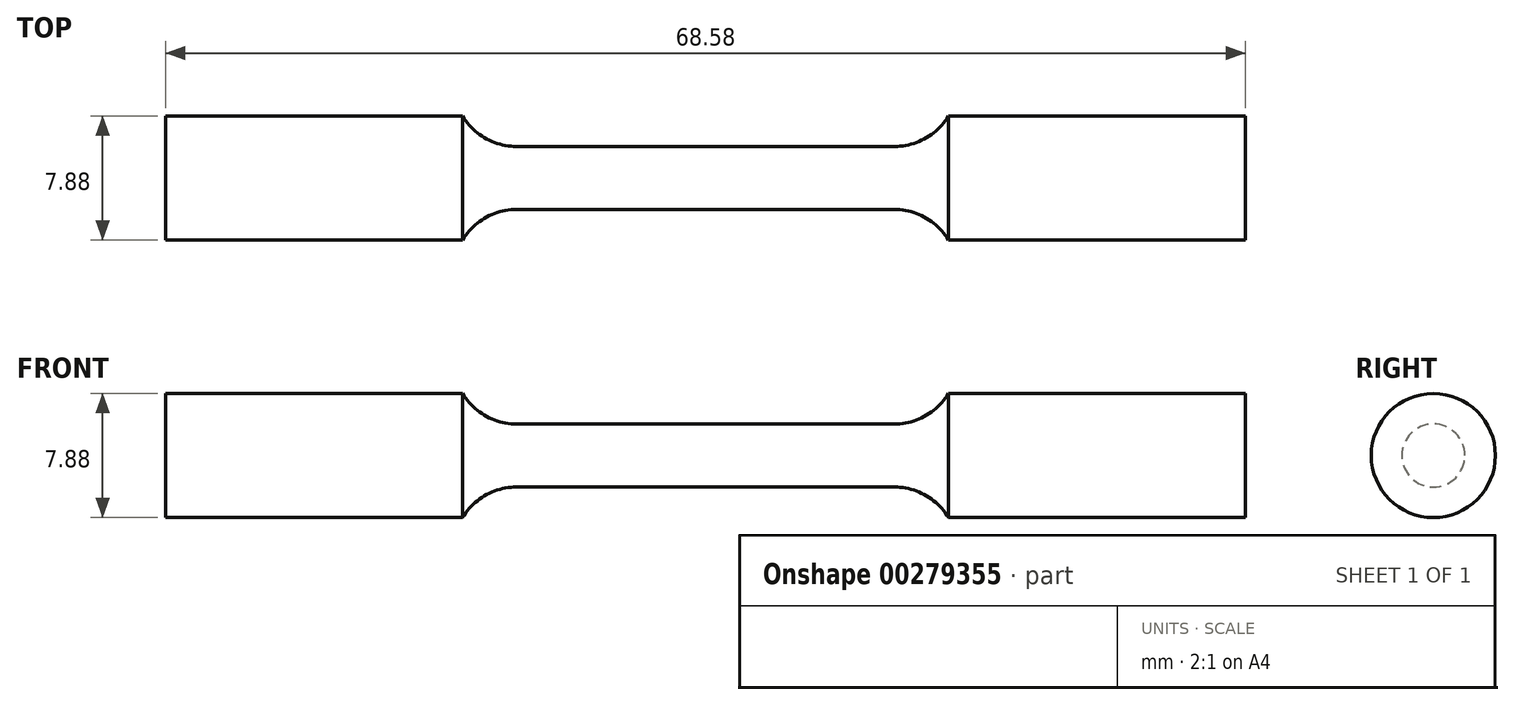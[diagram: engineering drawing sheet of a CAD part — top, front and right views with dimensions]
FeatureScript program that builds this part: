
annotation { "Feature Type Name" : "Feature", "Feature Type Description" : "" }
export const myFeature = defineFeature(function(context is Context, id is Id, definition is map)
    precondition{}
    {
        {
            var Q0;
            Q0=qCreatedBy(makeId("Front.planeOp"),FACE);
            var sketch = newSketch(context, id + "F0", { "sketchPlane" : qUnion([Q0])});
            skLineSegment(sketch, "E0", {"start": v(0, 2) * mm, "end": v(12, 2) * mm});
            skArc(sketch, "E1", {"start": v(12, 2) * mm, "mid": v(13.97, 2.52) * mm, "end": v(15.43, 3.94) * mm});
            skLineSegment(sketch, "E2", {"start": v(15.43, 3.94) * mm, "end": v(34.29, 3.94) * mm});
            skLineSegment(sketch, "E3", {"start": v(34.29, 3.94) * mm, "end": v(34.29, 0) * mm});
            skLineSegment(sketch, "E4.MirrorCS", {"start": v(0, 2) * mm, "end": v(-12, 2) * mm});
            skLineSegment(sketch, "E5.MirrorCS", {"start": v(-34.29, 3.94) * mm, "end": v(-34.29, 0) * mm});
            skLineSegment(sketch, "E6.MirrorCS", {"start": v(-15.43, 3.94) * mm, "end": v(-34.29, 3.94) * mm});
            skArc(sketch, "E7.MirrorCS", {"start": v(-12, 2) * mm, "mid": v(-13.97, 2.52) * mm, "end": v(-15.43, 3.94) * mm});
            skLineSegment(sketch, "E8", {"start": v(-34.29, 0) * mm, "end": v(34.29, 0) * mm});
            skSolve(sketch);
        }
        {
            var Q0;
            Q0 = qSketchRegion(id + "F0", true);
            var Q1;
            Q1=sQuery(id+"F0.wireOp",EDGE,"E8");
            revolve(context, id + "F1", {"entities" : qUnion([Q0]), "axis" : qUnion([Q1]), "revolveType" : RevolveType.FULL});
        }
    });
